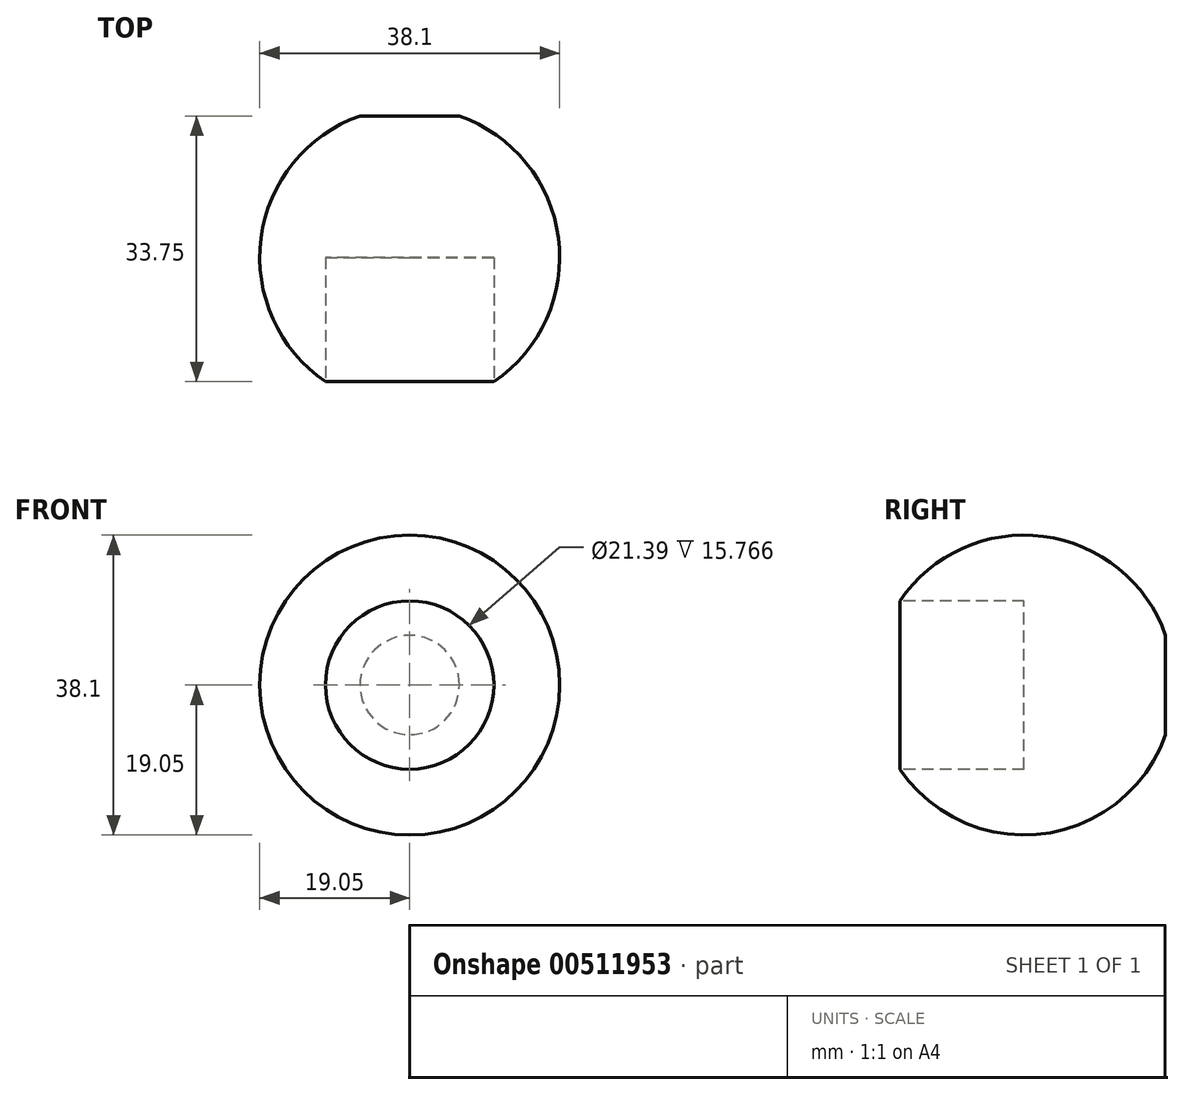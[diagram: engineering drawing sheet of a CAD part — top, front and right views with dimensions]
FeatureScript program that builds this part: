
annotation { "Feature Type Name" : "Feature", "Feature Type Description" : "" }
export const myFeature = defineFeature(function(context is Context, id is Id, definition is map)
    precondition{}
    {
        {
            var Q0;
            Q0=qCreatedBy(makeId("Top.planeOp"),FACE);
            var sketch = newSketch(context, id + "F0", { "sketchPlane" : qUnion([Q0])});
            skLineSegment(sketch, "E0", {"start": v(-10.7, -15.77) * mm, "end": v(-10.7, 0) * mm});
            skLineSegment(sketch, "E1", {"start": v(-10.7, 0) * mm, "end": v(10.7, 0) * mm, "construction": true});
            skLineSegment(sketch, "E2", {"start": v(10.7, 0) * mm, "end": v(10.7, -15.77) * mm, "construction": true});
            skLineSegment(sketch, "E3", {"start": v(0, -19.05) * mm, "end": v(0, 19.05) * mm, "construction": true});
            skLineSegment(sketch, "E4", {"start": v(-10.7, 0) * mm, "end": v(0, 0) * mm});
            skLineSegment(sketch, "E5", {"start": v(0, 0) * mm, "end": v(0, 19.05) * mm});
            skArc(sketch, "E6", {"start": v(0, 19.05) * mm, "mid": v(-18.21, 5.6) * mm, "end": v(-10.7, -15.77) * mm, "construction": true});
            skLineSegment(sketch, "E7", {"start": v(0, 17.98) * mm, "end": v(-6.3, 17.98) * mm});
            skArc(sketch, "E8", {"start": v(-6.3, 17.98) * mm, "mid": v(-18.9, 2.46) * mm, "end": v(-10.7, -15.77) * mm});
            skSolve(sketch);
        }
        {
            var Q0;
            Q0=makeQuery(id+"F0.imprint","IMPRINT",FACE,{"disambiguationData":[TD([[makeQuery(id+"F0.imprint","IMPRINT",EDGE,{"derivedFrom":sQuery(id+"F0.wireOp",EDGE,"E0")}),1.0]])]});
            var Q1;
            Q1=sQuery(id+"F0.wireOp",EDGE,"E3");
            revolve(context, id + "F1", {"entities" : qUnion([Q0]), "axis" : qUnion([Q1]), "revolveType" : RevolveType.FULL});
        }
    });
